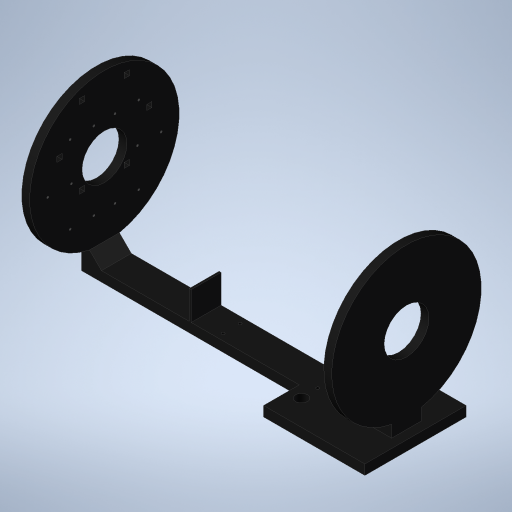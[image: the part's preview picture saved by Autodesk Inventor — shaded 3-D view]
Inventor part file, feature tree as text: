
AUTODESK INVENTOR PART (.ipt)
format: ipt  version: 2023 (Build 270158000, 158)  size: 562,176 bytes
history: native  units: in
note: dims shown in document units (in); Inventor stores cm internally (conversion verified against a paired STEP export)
features: extrude x13, sketch x6, projected_geometry x2, pattern_linear x1
ambient origin geometry x8: Origin, YZ Plane, XZ Plane, XY Plane, X Axis, Y Axis, Z Axis, Center Point
bodies: Solid1 (feature_tree)
feature tree (22):
  extrude  "Extrusion1"  Depth=0.2047in
  extrude  "Extrusion2"  Depth=0.2047in TaperAngle=360.0deg
  extrude  "Extrusion3"  Depth=0.315in
  sketch  "Sketch2"  dims[d31=0.2047in d32=2.3622in d34=360.0deg]
  extrude  "Extrusion4"  Depth=0.2047in
  extrude  "Extrusion5"  Depth=0.315in
  pattern_linear  "Rectangular Pattern1"  Spacing1=0.2047in  [1 undecoded]
  extrude  "Extrusion7"  Depth=1.1811in
  extrude  "Extrusion8"  Depth=4.3307in
  extrude  "Extrusion9"  Depth=1.1811in
  sketch  "Sketch7"  dims[d40=0.315in d41=0.315in]
  extrude  "Extrusion11"  Depth=1.1811in
  extrude  "Extrusion12"  Depth=0.315in
  extrude  "Extrusion13"  Depth=1.122in
  extrude  "Extrusion10"  Depth=0.3937in
  extrude  "Extrusion6"  Depth=0.315in TaperAngle=0.0deg
  sketch  "Sketch3"  dims[d36=0.315in d37=0.315in]
  projected_geometry  "Projected Loop1"
  sketch  "Sketch4"  dims[d38=0.2047in d39=0.2047in]
  projected_geometry  "Projected Loop2"
  sketch  "Sketch8"  dims[d42=0.2047in d43=0.2047in d44=0.8465in d45=4.3307in d46=2.7559in d47=0.5906in d49=0.315in d50=1.122in d51=0.3937in d52=0.315in d53=0.0in d54=0.3937in d55=0.0in d56=12.5984in d57=0.0in d58=4.0in d59=4.0in d60=0.4724in d63=0.2559in d65=4.0157in d66=1.0039in d67=0.3346in d68=0.1181in d69=0.7874in d71=3.7402in d72=0.3937in d74=0.3937in d76=0.3937in d77=0.0in d78=0.3937in d79=0.0in d80=1.0in d81=0.5in d82=3.0118in d83=0.3937in d84=0.0in d85=0.7874in d87=11.9291in d88=0.122in d89=0.0in d90=0.122in d91=0.0in d92=0.0787in d93=1.5157in d94=0.0in d95=2.3622in d97=360.0deg d99=120.0deg d102=120.0deg d105=120.0deg d108=1.7717in d109=5.9055in d110=0.315in d111=0.0in d112=1.7717in d113=5.9055in d114=0.3937in d115=0.0in d116=0.2717in d117=0.0in d118=0.9843in d119=0.7283in d120=0.0827in d122=0.5413in d123=2.3622in d125=360.0deg d127=0.0827in d128=0.5413in d129=0.0827in d130=0.5413in d131=0.0787in d132=45.0deg d133=45.0deg d134=1.1811in d135=0.0in]
  sketch  "Sketch1"  dims[d8=1.378in d9=1.7717in d12=1.1811in d13=0.315in d14=0.315in d22=1.1811in d23=0.315in d24=1.1811in d25=1.378in d26=1.378in d27=0.1575in d30=0.2047in]
note: 1 required parameter value undecoded (feature->parameter linkage not recoverable at this tier; creation-order binding heuristic only, values carry confidence <= 0.55)
